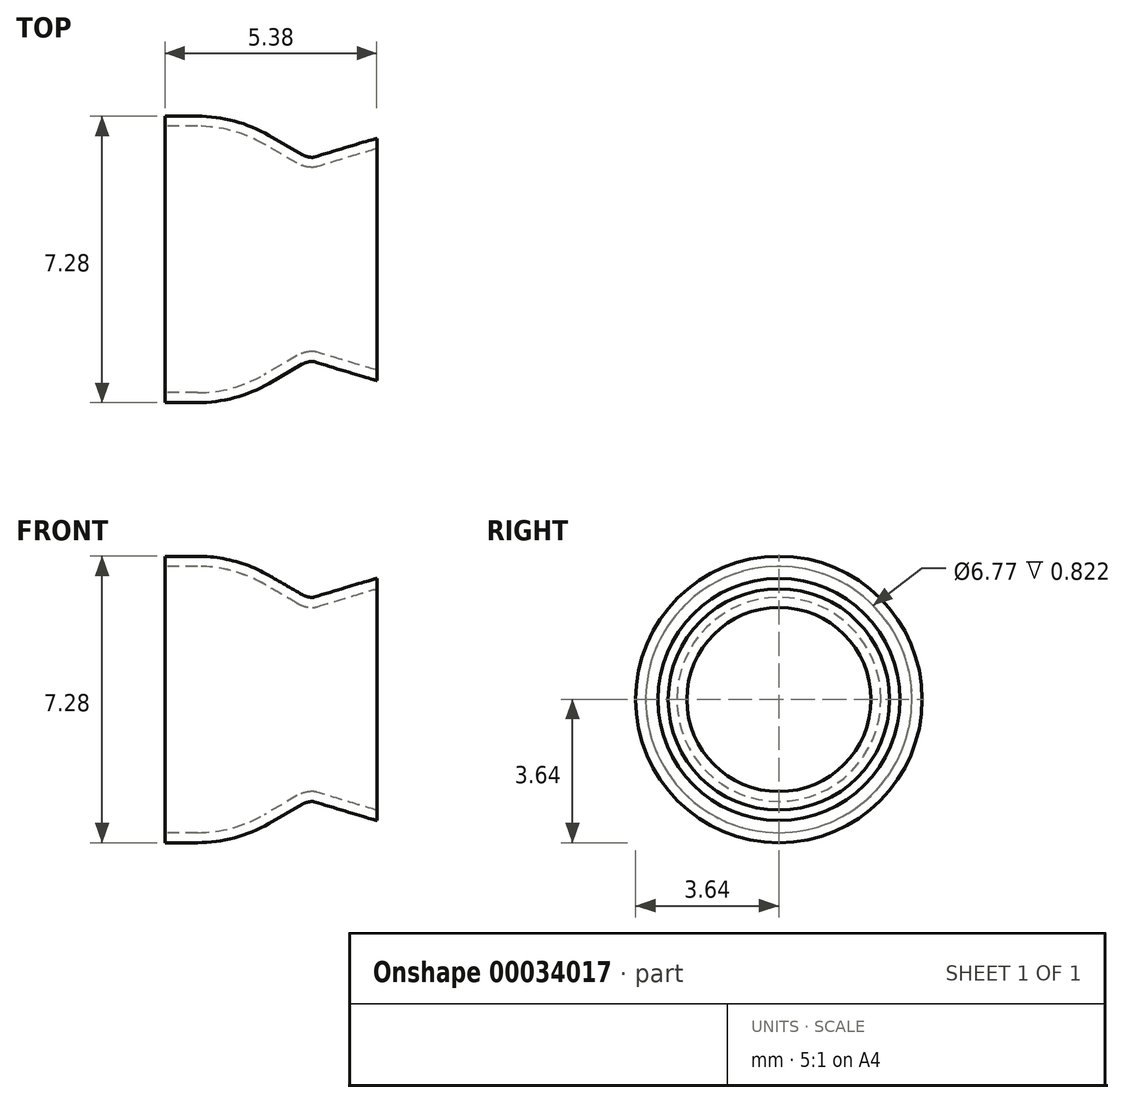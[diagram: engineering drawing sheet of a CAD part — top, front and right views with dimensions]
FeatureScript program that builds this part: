
annotation { "Feature Type Name" : "Feature", "Feature Type Description" : "" }
export const myFeature = defineFeature(function(context is Context, id is Id, definition is map)
    precondition{}
    {
        {
            var Q0;
            Q0=qCreatedBy(makeId("Front.planeOp"),FACE);
            var sketch = newSketch(context, id + "F0", { "sketchPlane" : qUnion([Q0])});
            skLineSegment(sketch, "E0", {"start": v(-2.7, 0.52) * mm, "end": v(-1.87, 0.52) * mm});
            skArc(sketch, "E1", {"start": v(-0.05, 0.03) * mm, "mid": v(-0.93, 0.4) * mm, "end": v(-1.87, 0.52) * mm});
            skLineSegment(sketch, "E2", {"start": v(-0.05, 0.03) * mm, "end": v(0.8, -0.45) * mm});
            skArc(sketch, "E3", {"start": v(0.8, -0.45) * mm, "mid": v(0.92, -0.5) * mm, "end": v(1.06, -0.52) * mm});
            skArc(sketch, "E4", {"start": v(1.06, -0.52) * mm, "mid": v(1.08, -0.52) * mm, "end": v(1.1, -0.52) * mm});
            skFitSpline(sketch, "E5", {"points": [v(1.1, -0.52) * mm, v(2.54, -0.08) * mm, v(2.7, -0.04) * mm]});
            skLineSegment(sketch, "E6", {"start": v(-2.7, 0.52) * mm, "end": v(-2.7, -3.12) * mm});
            skLineSegment(sketch, "E7", {"start": v(-2.7, -3.12) * mm, "end": v(2.7, -3.12) * mm});
            skLineSegment(sketch, "E8", {"start": v(2.7, -0.04) * mm, "end": v(2.7, -3.12) * mm});
            skSolve(sketch);
        }
        {
            var Q0;
            Q0 = qSketchRegion(id + "F0", true);
            var Q1;
            Q1=sQuery(id+"F0.wireOp",EDGE,"E7");
            revolve(context, id + "F1", {"entities" : qUnion([Q0]), "axis" : qUnion([Q1]), "revolveType" : RevolveType.FULL});
        }
        {
            var Q0;
            Q0=makeQuery(id+"F1.opRevolve","SWEPT_FACE",FACE,{"disambiguationData":[OSD([sQuery(id+"F0.wireOp",EDGE,"E6")])]});
            var sketch = newSketch(context, id + "F2", { "sketchPlane" : qUnion([Q0])});
            skPoint(sketch, "E9", {"position": v(0, -3.12) * mm});
            skSolve(sketch);
        }
        {
            var Q0;
            Q0=makeQuery(id+"F1.opRevolve","SWEPT_BODY",BODY,{"disambiguationData":[OSD([sQuery(id+"F0.wireOp",EDGE,"E0"),sQuery(id+"F0.wireOp",EDGE,"E1"),sQuery(id+"F0.wireOp",EDGE,"E2"),sQuery(id+"F0.wireOp",EDGE,"E3"),sQuery(id+"F0.wireOp",EDGE,"E4"),sQuery(id+"F0.wireOp",EDGE,"E5"),sQuery(id+"F0.wireOp",EDGE,"E6"),sQuery(id+"F0.wireOp",EDGE,"E7"),sQuery(id+"F0.wireOp",EDGE,"E8")])]});
            var Q1;
            Q1=sQuery(id+"F2.wireOp",VERTEX,"E9");
            var Q2;
            Q2=qCreatedBy(makeId("Origin.pointOp"),VERTEX);
            transform(context, id + "F3", {"entities" : qUnion([Q0]), "transformType" : TransformType.TRANSLATION_ENTITY, "oppositeDirectionEntity" : false, "transformLine" : qUnion([Q1, Q2]), "makeCopy" : false});
        }
        {
            var Q0;
            Q0=makeQuery(id+"F1.opRevolve","SWEPT_FACE",FACE,{"disambiguationData":[OSD([sQuery(id+"F0.wireOp",EDGE,"E6")])]});
            var Q1;
            Q1=makeQuery(id+"F1.opRevolve","SWEPT_FACE",FACE,{"disambiguationData":[OSD([sQuery(id+"F0.wireOp",EDGE,"E8")])]});
            shell(context, id + "F4", {"entities" : qUnion([Q0, Q1]), "thickness" : 0.25 * mm});
        }
    });
